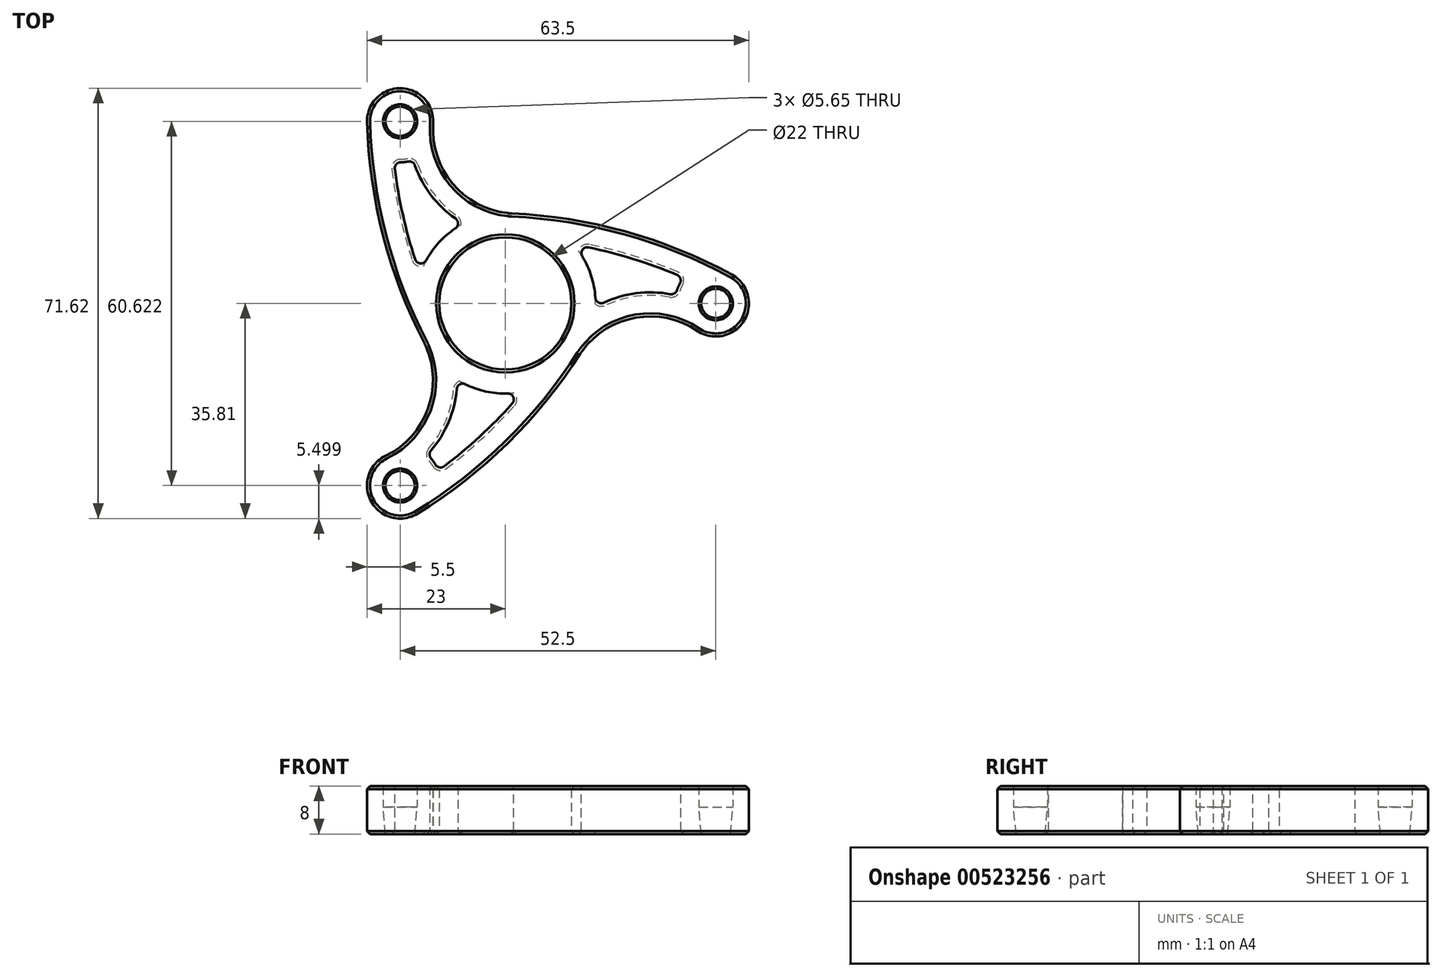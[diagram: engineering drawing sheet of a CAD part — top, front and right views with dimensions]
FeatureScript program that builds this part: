
annotation { "Feature Type Name" : "Feature", "Feature Type Description" : "" }
export const myFeature = defineFeature(function(context is Context, id is Id, definition is map)
    precondition{}
    {
        {
            var Q0;
            Q0=qCreatedBy(makeId("Top.planeOp"),FACE);
            var sketch = newSketch(context, id + "F0", { "sketchPlane" : qUnion([Q0])});
            skCircle(sketch, "E0", {"center": v(0, 0) * mm, "radius": 11 * mm});
            skArc(sketch, "E1.0", {"start": v(0.6, 14.99) * mm, "mid": v(-13.37, -6.8) * mm, "end": v(12.46, -8.36) * mm});
            skLineSegment(sketch, "E2", {"start": v(0, 0) * mm, "end": v(35, 0) * mm, "construction": true});
            skArc(sketch, "E3", {"start": v(31.92, -4.56) * mm, "mid": v(39.7, -2.85) * mm, "end": v(37.61, 4.84) * mm});
            skArc(sketch, "E4", {"start": v(31.92, -4.56) * mm, "mid": v(21.4, -2.42) * mm, "end": v(12.46, -8.36) * mm});
            skArc(sketch, "E5", {"start": v(37.61, 4.84) * mm, "mid": v(19.69, 12.03) * mm, "end": v(0.6, 14.99) * mm});
            skSolve(sketch);
        }
        {
            var Q0;
            Q0=makeQuery(id+"F0.imprint","IMPRINT",FACE,{"disambiguationData":[TD([[makeQuery(id+"F0.imprint","IMPRINT",EDGE,{"derivedFrom":sQuery(id+"F0.wireOp",EDGE,"E0")}),-1.0]])]});
            extrude(context, id + "F1", {"entities" : qUnion([Q0]), "endBound" : BoundingType.SYMMETRIC, "depth" : 8 * mm, "offsetDistance" : 25 * mm});
        }
        {
            var Q0;
            Q0=qCreatedBy(makeId("Front.planeOp"),FACE);
            var sketch = newSketch(context, id + "F2", { "sketchPlane" : qUnion([Q0])});
            skLineSegment(sketch, "E6", {"start": v(35, 5.95) * mm, "end": v(35, -6.38) * mm, "construction": true});
            skLineSegment(sketch, "E7", {"start": v(35, 4) * mm, "end": v(37.83, 4) * mm});
            skLineSegment(sketch, "E8", {"start": v(37.83, 4) * mm, "end": v(37.83, 0.5) * mm});
            skLineSegment(sketch, "E9", {"start": v(37.83, 0.5) * mm, "end": v(37.43, -4) * mm});
            skLineSegment(sketch, "E10", {"start": v(37.43, -4) * mm, "end": v(35, -4) * mm});
            skLineSegment(sketch, "E11", {"start": v(35, -4) * mm, "end": v(35, 4) * mm});
            skSolve(sketch);
        }
        {
            var Q0;
            Q0 = qSketchRegion(id + "F2", true);
            var Q1;
            Q1=sQuery(id+"F2.wireOp",EDGE,"E6");
            revolve(context, id + "F3", {"operationType" : NewBodyOperationType.REMOVE, "entities" : qUnion([Q0]), "axis" : qUnion([Q1]), "revolveType" : RevolveType.FULL, "oppositeDirection" : true});
        }
        {
            var Q0;
            Q0=makeQuery(id+"F1.opExtrude","CAP_FACE",FACE,{"disambiguationData":[OSD([sQuery(id+"F0.wireOp",EDGE,"E0"),sQuery(id+"F0.wireOp",EDGE,"E1.0"),sQuery(id+"F0.wireOp",EDGE,"E3"),sQuery(id+"F0.wireOp",EDGE,"E4"),sQuery(id+"F0.wireOp",EDGE,"E5")])],"isStart":false});
            var sketch = newSketch(context, id + "F4", { "sketchPlane" : qUnion([Q0])});
            skArc(sketch, "E12.0", {"start": v(14.99, -0.62) * mm, "mid": v(21.46, 1.65) * mm, "end": v(28.3, 1.34) * mm});
            skArc(sketch, "E12.2", {"start": v(29.67, 4.27) * mm, "mid": v(20.67, 7.58) * mm, "end": v(11.34, 9.81) * mm});
            skArc(sketch, "E13.0", {"start": v(14.99, -0.62) * mm, "mid": v(14.16, 4.94) * mm, "end": v(11.34, 9.81) * mm});
            skArc(sketch, "E14.0", {"start": v(29.67, 4.27) * mm, "mid": v(28.81, 2.89) * mm, "end": v(28.3, 1.34) * mm});
            skSolve(sketch);
        }
        {
            var Q0;
            Q0 = qSketchRegion(id + "F4", true);
            extrude(context, id + "F5", {"entities" : qUnion([Q0]), "operationType" : NewBodyOperationType.REMOVE, "oppositeDirection" : true, "depth" : 25 * mm, "offsetDistance" : 25 * mm});
        }
        {
            var Q0;
            Q0=makeQuery(id+"F5.boolean.opBoolean","COPY",EDGE,{"derivedFrom":makeQuery(id+"F5.opExtrude","SWEPT_EDGE",EDGE,{"disambiguationData":[OSD([sQuery(id+"F4.wireOp",EDGE,"E12.0"),sQuery(id+"F4.wireOp",EDGE,"E13.0")])]})});
            var Q1;
            Q1=makeQuery(id+"F5.boolean.opBoolean","COPY",EDGE,{"derivedFrom":makeQuery(id+"F5.opExtrude","SWEPT_EDGE",EDGE,{"disambiguationData":[OSD([sQuery(id+"F4.wireOp",EDGE,"E12.2"),sQuery(id+"F4.wireOp",EDGE,"E13.0")])]})});
            var Q2;
            Q2=makeQuery(id+"F5.boolean.opBoolean","COPY",EDGE,{"derivedFrom":makeQuery(id+"F5.opExtrude","SWEPT_EDGE",EDGE,{"disambiguationData":[OSD([sQuery(id+"F4.wireOp",EDGE,"E12.0"),sQuery(id+"F4.wireOp",EDGE,"E14.0")])]})});
            var Q3;
            Q3=makeQuery(id+"F5.boolean.opBoolean","COPY",EDGE,{"derivedFrom":makeQuery(id+"F5.opExtrude","SWEPT_EDGE",EDGE,{"disambiguationData":[OSD([sQuery(id+"F4.wireOp",EDGE,"E12.2"),sQuery(id+"F4.wireOp",EDGE,"E14.0")])]})});
            fillet(context, id + "F6", {"entities" : qUnion([Q0, Q1, Q2, Q3]), "radius" : 1 * mm, "tangentPropagation" : true, "allowEdgeOverflow" : false});
        }
        {
            var Q0;
            Q0=makeQuery(id+"F5.boolean.opBoolean","COPY",EDGE,{"derivedFrom":makeQuery(id+"F5.opExtrude","CAP_EDGE",EDGE,{"disambiguationData":[OSD([sQuery(id+"F4.wireOp",EDGE,"E12.0")])],"isStart":true})});
            var Q1;
            Q1=makeQuery(id+"F5.boolean.opBoolean","COPY",EDGE,{"derivedFrom":makeQuery(id+"F5.opExtrude","CAP_EDGE",EDGE,{"disambiguationData":[OSD([sQuery(id+"F4.wireOp",EDGE,"E13.0")])],"isStart":true})});
            var Q2;
            Q2=makeQuery(id+"F5.boolean.opBoolean","COPY",EDGE,{"derivedFrom":makeQuery(id+"F5.opExtrude","CAP_EDGE",EDGE,{"disambiguationData":[OSD([sQuery(id+"F4.wireOp",EDGE,"E12.2")])],"isStart":true})});
            var Q3;
            Q3=makeQuery(id+"F5.boolean.opBoolean","COPY",EDGE,{"derivedFrom":makeQuery(id+"F5.opExtrude","CAP_EDGE",EDGE,{"disambiguationData":[OSD([sQuery(id+"F4.wireOp",EDGE,"E14.0")])],"isStart":true})});
            var Q4;
            Q4=makeQuery(id+"F1.opExtrude","CAP_EDGE",EDGE,{"disambiguationData":[OSD([sQuery(id+"F0.wireOp",EDGE,"E0")])],"isStart":false});
            var Q5;
            Q5=makeQuery(id+"F5.boolean.opBoolean","INTERSECT",EDGE,{"derivedFrom":[makeQuery(id+"F1.opExtrude","CAP_FACE",FACE,{"disambiguationData":[OSD([sQuery(id+"F0.wireOp",EDGE,"E0"),sQuery(id+"F0.wireOp",EDGE,"E1.0"),sQuery(id+"F0.wireOp",EDGE,"E3"),sQuery(id+"F0.wireOp",EDGE,"E4"),sQuery(id+"F0.wireOp",EDGE,"E5")])],"isStart":true}),makeQuery(id+"F5.opExtrude","SWEPT_FACE",FACE,{"disambiguationData":[OSD([sQuery(id+"F4.wireOp",EDGE,"E12.2")])]})]});
            var Q6;
            Q6=makeQuery(id+"F5.boolean.opBoolean","INTERSECT",EDGE,{"derivedFrom":[makeQuery(id+"F1.opExtrude","CAP_FACE",FACE,{"disambiguationData":[OSD([sQuery(id+"F0.wireOp",EDGE,"E0"),sQuery(id+"F0.wireOp",EDGE,"E1.0"),sQuery(id+"F0.wireOp",EDGE,"E3"),sQuery(id+"F0.wireOp",EDGE,"E4"),sQuery(id+"F0.wireOp",EDGE,"E5")])],"isStart":true}),makeQuery(id+"F5.opExtrude","SWEPT_FACE",FACE,{"disambiguationData":[OSD([sQuery(id+"F4.wireOp",EDGE,"E12.0")])]})]});
            var Q7;
            Q7=makeQuery(id+"F5.boolean.opBoolean","INTERSECT",EDGE,{"derivedFrom":[makeQuery(id+"F1.opExtrude","CAP_FACE",FACE,{"disambiguationData":[OSD([sQuery(id+"F0.wireOp",EDGE,"E0"),sQuery(id+"F0.wireOp",EDGE,"E1.0"),sQuery(id+"F0.wireOp",EDGE,"E3"),sQuery(id+"F0.wireOp",EDGE,"E4"),sQuery(id+"F0.wireOp",EDGE,"E5")])],"isStart":true}),makeQuery(id+"F5.opExtrude","SWEPT_FACE",FACE,{"disambiguationData":[OSD([sQuery(id+"F4.wireOp",EDGE,"E14.0")])]})]});
            var Q8;
            Q8=makeQuery(id+"F1.opExtrude","CAP_EDGE",EDGE,{"disambiguationData":[OSD([sQuery(id+"F0.wireOp",EDGE,"E0")])],"isStart":true});
            var Q9;
            Q9=makeQuery(id+"F5.boolean.opBoolean","INTERSECT",EDGE,{"derivedFrom":[makeQuery(id+"F1.opExtrude","CAP_FACE",FACE,{"disambiguationData":[OSD([sQuery(id+"F0.wireOp",EDGE,"E0"),sQuery(id+"F0.wireOp",EDGE,"E1.0"),sQuery(id+"F0.wireOp",EDGE,"E3"),sQuery(id+"F0.wireOp",EDGE,"E4"),sQuery(id+"F0.wireOp",EDGE,"E5")])],"isStart":true}),makeQuery(id+"F5.opExtrude","SWEPT_FACE",FACE,{"disambiguationData":[OSD([sQuery(id+"F4.wireOp",EDGE,"E13.0")])]})]});
            var Q10;
            Q10=makeQuery(id+"F3.boolean.opBoolean","COPY",EDGE,{"derivedFrom":makeQuery(id+"F3.opRevolve","SWEPT_EDGE",EDGE,{"disambiguationData":[OSD([sQuery(id+"F2.wireOp",EDGE,"E7"),sQuery(id+"F2.wireOp",EDGE,"E8")])]})});
            chamfer(context, id + "F7", {"entities" : qUnion([Q0, Q1, Q2, Q3, Q4, Q5, Q6, Q7, Q8, Q9, Q10]), "width" : .5 * mm, "tangentPropagation" : true});
        }
        {
            var Q0;
            Q0=makeQuery(id+"F1.opExtrude","SWEPT_BODY",BODY,{"disambiguationData":[OSD([sQuery(id+"F0.wireOp",EDGE,"E0"),sQuery(id+"F0.wireOp",EDGE,"E1.0"),sQuery(id+"F0.wireOp",EDGE,"E3"),sQuery(id+"F0.wireOp",EDGE,"E4"),sQuery(id+"F0.wireOp",EDGE,"E5")])]});
            var Q1;
            Q1=makeQuery(id+"F1.opExtrude","SWEPT_FACE",FACE,{"disambiguationData":[OSD([sQuery(id+"F0.wireOp",EDGE,"E0")])]});
            circularPattern(context, id + "F8", {"operationType" : NewBodyOperationType.ADD, "entities" : qUnion([Q0]), "axis" : qUnion([Q1]), "angle" : 360 * degree, "instanceCount" : 3, "equalSpace" : true});
        }
        {
            var Q0;
            Q0=makeQuery(id+"F8.boolean.opBoolean","INTERSECT",EDGE,{"derivedFrom":[makeQuery(id+"F1.opExtrude","SWEPT_FACE",FACE,{"disambiguationData":[OSD([sQuery(id+"F0.wireOp",EDGE,"E4")])]}),makeQuery(id+"F8.opPattern","COPY",FACE,{"derivedFrom":makeQuery(id+"F1.opExtrude","SWEPT_FACE",FACE,{"disambiguationData":[OSD([sQuery(id+"F0.wireOp",EDGE,"E5")])]}),"instanceName":"2"})]});
            var Q1;
            Q1=makeQuery(id+"F8.boolean.opBoolean","INTERSECT",EDGE,{"derivedFrom":[makeQuery(id+"F1.opExtrude","SWEPT_FACE",FACE,{"disambiguationData":[OSD([sQuery(id+"F0.wireOp",EDGE,"E5")])]}),makeQuery(id+"F8.opPattern","COPY",FACE,{"derivedFrom":makeQuery(id+"F1.opExtrude","SWEPT_FACE",FACE,{"disambiguationData":[OSD([sQuery(id+"F0.wireOp",EDGE,"E4")])]}),"instanceName":"1"})]});
            var Q2;
            Q2=makeQuery(id+"F8.boolean.opBoolean","INTERSECT",EDGE,{"derivedFrom":[makeQuery(id+"F8.opPattern","COPY",FACE,{"derivedFrom":makeQuery(id+"F1.opExtrude","SWEPT_FACE",FACE,{"disambiguationData":[OSD([sQuery(id+"F0.wireOp",EDGE,"E5")])]}),"instanceName":"1"}),makeQuery(id+"F8.opPattern","COPY",FACE,{"derivedFrom":makeQuery(id+"F1.opExtrude","SWEPT_FACE",FACE,{"disambiguationData":[OSD([sQuery(id+"F0.wireOp",EDGE,"E4")])]}),"instanceName":"2"})]});
            fillet(context, id + "F9", {"entities" : qUnion([Q0, Q1, Q2]), "radius" : 10 * mm, "tangentPropagation" : true, "allowEdgeOverflow" : false});
        }
        {
            var Q0;
            Q0=makeQuery(id+"F1.opExtrude","CAP_EDGE",EDGE,{"disambiguationData":[OSD([sQuery(id+"F0.wireOp",EDGE,"E5")])],"isStart":false});
            var Q1;
            Q1=makeQuery(id+"F1.opExtrude","CAP_EDGE",EDGE,{"disambiguationData":[OSD([sQuery(id+"F0.wireOp",EDGE,"E5")])],"isStart":true});
            chamfer(context, id + "F10", {"entities" : qUnion([Q0, Q1]), "width" : .5 * mm, "tangentPropagation" : true});
        }
    });
